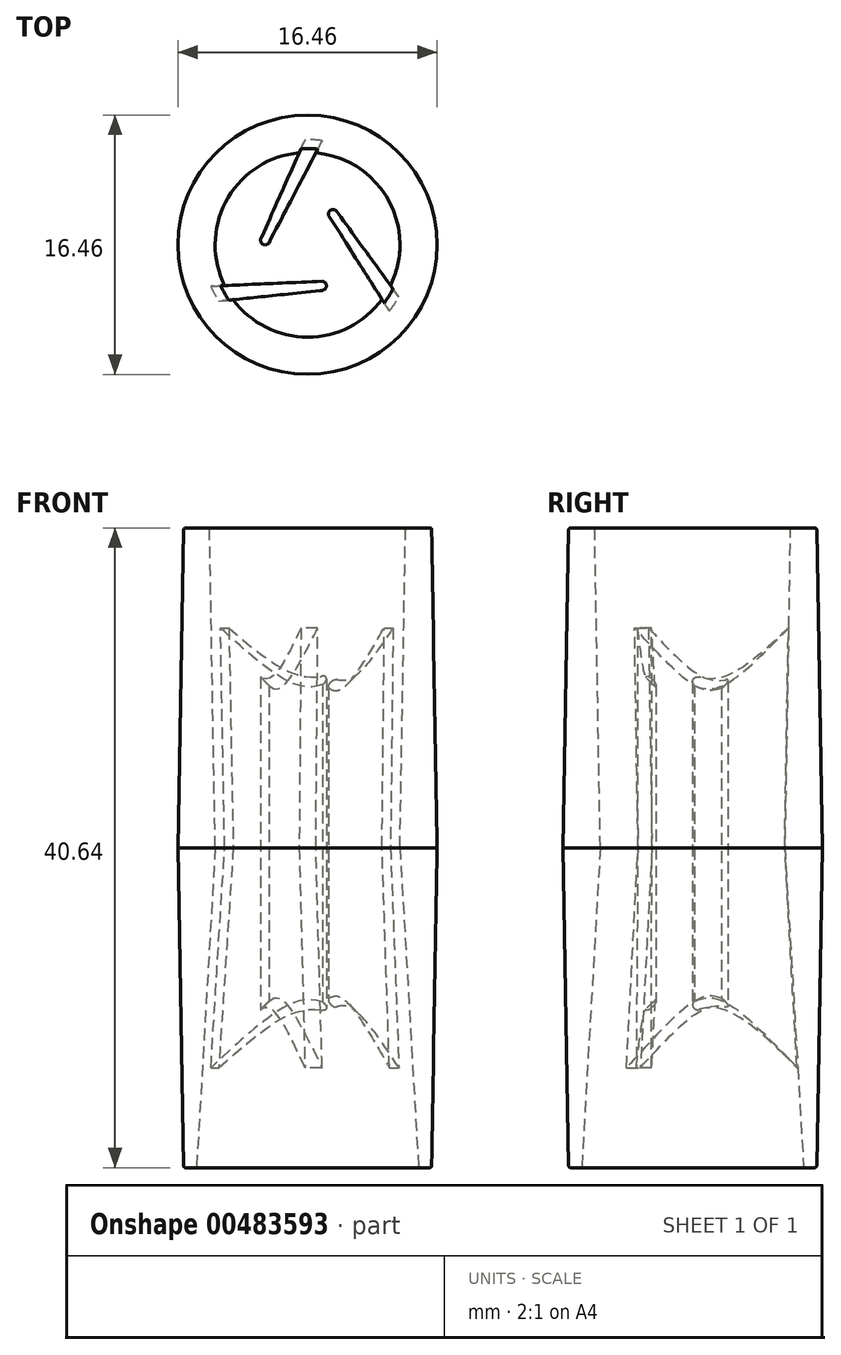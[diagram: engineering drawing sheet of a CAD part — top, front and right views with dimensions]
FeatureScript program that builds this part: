
annotation { "Feature Type Name" : "Feature", "Feature Type Description" : "" }
export const myFeature = defineFeature(function(context is Context, id is Id, definition is map)
    precondition{}
    {
        {
            var Q0;
            Q0=qCreatedBy(makeId("Front.planeOp"),FACE);
            var sketch = newSketch(context, id + "F0", { "sketchPlane" : qUnion([Q0])});
            skLineSegment(sketch, "E0", {"start": v(0, 30.91) * mm, "end": v(0, -20.42) * mm, "construction": true});
            skLineSegment(sketch, "E1", {"start": v(-15.28, 0) * mm, "end": v(16.53, 0) * mm, "construction": true});
            skLineSegment(sketch, "E2", {"start": v(8.23, 0) * mm, "end": v(7.88, -20.2) * mm});
            skLineSegment(sketch, "E3", {"start": v(7.75, -20.32) * mm, "end": v(7.17, -20.32) * mm});
            skLineSegment(sketch, "E4", {"start": v(7.04, -20.2) * mm, "end": v(5.87, 0) * mm});
            skLineSegment(sketch, "E5", {"start": v(5.87, 0) * mm, "end": v(6.22, 20.2) * mm});
            skLineSegment(sketch, "E6", {"start": v(6.35, 20.32) * mm, "end": v(7.75, 20.32) * mm});
            skLineSegment(sketch, "E7", {"start": v(8.23, 0) * mm, "end": v(7.88, 20.2) * mm});
            skPoint(sketch, "E8.visualSharp", {"position": v(7.87, -20.32) * mm});
            skArc(sketch, "E8.filletArc", {"start": v(7.75, -20.32) * mm, "mid": v(7.84, -20.28) * mm, "end": v(7.88, -20.2) * mm});
            skPoint(sketch, "E9.visualSharp", {"position": v(7.05, -20.32) * mm});
            skArc(sketch, "E9.filletArc", {"start": v(7.04, -20.2) * mm, "mid": v(7.08, -20.29) * mm, "end": v(7.17, -20.32) * mm});
            skPoint(sketch, "E10.visualSharp", {"position": v(6.22, 20.32) * mm});
            skArc(sketch, "E10.filletArc", {"start": v(6.35, 20.32) * mm, "mid": v(6.26, 20.28) * mm, "end": v(6.22, 20.2) * mm});
            skPoint(sketch, "E11.visualSharp", {"position": v(7.87, 20.32) * mm});
            skArc(sketch, "E11.filletArc", {"start": v(7.88, 20.2) * mm, "mid": v(7.84, 20.28) * mm, "end": v(7.75, 20.32) * mm});
            skPoint(sketch, "E12", {"position": v(6.68, -13.97) * mm});
            skPoint(sketch, "E13", {"position": v(6.11, 13.97) * mm});
            skSolve(sketch);
        }
        {
            var Q0;
            Q0=makeQuery(id+"F0.imprint","IMPRINT",FACE,{"disambiguationData":[TD([[makeQuery(id+"F0.imprint","IMPRINT",EDGE,{"derivedFrom":sQuery(id+"F0.wireOp",EDGE,"E2")}),-1.0]])]});
            var Q1;
            Q1=sQuery(id+"F0.wireOp",EDGE,"E0");
            revolve(context, id + "F1", {"entities" : qUnion([Q0]), "axis" : qUnion([Q1]), "revolveType" : RevolveType.FULL});
        }
        {
            var Q0;
            Q0=qCreatedBy(makeId("Top.planeOp"),FACE);
            var sketch = newSketch(context, id + "F2", { "sketchPlane" : qUnion([Q0])});
            skCircle(sketch, "E14.0", {"center": v(-0.06, -0.12) * mm, "radius": 7.16 * mm});
            skCircle(sketch, "E15", {"center": v(-0.06, -0.12) * mm, "radius": 2.41 * mm, "construction": true});
            skLineSegment(sketch, "E16", {"start": v(1.1, 6.95) * mm, "end": v(-2.46, 0.11) * mm});
            skLineSegment(sketch, "E17", {"start": v(-2.9, 0.53) * mm, "end": v(0, 7.04) * mm});
            skArc(sketch, "E18", {"start": v(-2.96, 0.4) * mm, "mid": v(-2.84, 0.04) * mm, "end": v(-2.46, 0.11) * mm});
            skLineSegment(sketch, "E19.1.0", {"start": v(5.49, -4.66) * mm, "end": v(1.35, 1.84) * mm});
            skLineSegment(sketch, "E19.1.1", {"start": v(1.93, 2.02) * mm, "end": v(6.12, -3.75) * mm});
            skArc(sketch, "E19.1.2", {"start": v(1.85, 2.13) * mm, "mid": v(1.47, 2.21) * mm, "end": v(1.35, 1.84) * mm});
            skLineSegment(sketch, "E19.2.0", {"start": v(-6.76, -2.66) * mm, "end": v(0.94, -2.32) * mm});
            skLineSegment(sketch, "E19.2.1", {"start": v(0.8, -2.91) * mm, "end": v(-6.29, -3.65) * mm});
            skArc(sketch, "E19.2.2", {"start": v(0.93, -2.9) * mm, "mid": v(1.2, -2.61) * mm, "end": v(0.94, -2.32) * mm});
            skLineSegment(sketch, "E19.anchor1", {"start": v(-0.06, -0.12) * mm, "end": v(-2.46, 0.11) * mm, "construction": true});
            skLineSegment(sketch, "E19.anchor2", {"start": v(-0.06, -0.12) * mm, "end": v(0.94, -2.32) * mm, "construction": true});
            skLineSegment(sketch, "E20", {"start": v(1.85, 2.13) * mm, "end": v(1.93, 2.02) * mm});
            skLineSegment(sketch, "E21", {"start": v(-2.96, 0.4) * mm, "end": v(-2.9, 0.53) * mm});
            skLineSegment(sketch, "E22", {"start": v(0.93, -2.9) * mm, "end": v(0.8, -2.91) * mm});
            skSolve(sketch);
        }
        {
            var Q0;
            {var subQ0=sQuery(id+"F2.wireOp",EDGE,"E16");Q0=makeQuery(id+"F2.imprint","IMPRINT",FACE,{"disambiguationData":[TD([[makeQuery(id+"F2.imprint","IMPRINT",EDGE,{"derivedFrom":subQ0}),-1.0]])]});}
            var Q1;
            {var subQ0=sQuery(id+"F2.wireOp",EDGE,"E19.1.0");Q1=makeQuery(id+"F2.imprint","IMPRINT",FACE,{"disambiguationData":[TD([[makeQuery(id+"F2.imprint","IMPRINT",EDGE,{"derivedFrom":subQ0}),-1.0]])]});}
            var Q2;
            {var subQ0=sQuery(id+"F2.wireOp",EDGE,"E19.2.0");Q2=makeQuery(id+"F2.imprint","IMPRINT",FACE,{"disambiguationData":[TD([[makeQuery(id+"F2.imprint","IMPRINT",EDGE,{"derivedFrom":subQ0}),-1.0]])]});}
            extrude(context, id + "F3", {"entities" : qUnion([Q0, Q1, Q2]), "operationType" : NewBodyOperationType.ADD, "endBound" : BoundingType.SYMMETRIC, "depth" : 27.94 * mm, "offsetDistance" : 25.4 * mm});
        }
        {
            var Q0;
            Q0=qCreatedBy(makeId("Front.planeOp"),FACE);
            var sketch = newSketch(context, id + "F4", { "sketchPlane" : qUnion([Q0])});
            skPoint(sketch, "E23.0", {"position": v(6.68, -13.97) * mm});
            skPoint(sketch, "E24.0", {"position": v(6.11, 13.97) * mm});
            skLineSegment(sketch, "E25", {"start": v(0, -13.97) * mm, "end": v(6.68, -13.97) * mm});
            skLineSegment(sketch, "E26", {"start": v(0, -13.97) * mm, "end": v(0, -7.3) * mm});
            skLineSegment(sketch, "E27", {"start": v(0, -7.3) * mm, "end": v(6.68, -13.97) * mm});
            skLineSegment(sketch, "E28", {"start": v(0, 13.97) * mm, "end": v(6.11, 13.97) * mm});
            skLineSegment(sketch, "E29", {"start": v(0, 13.97) * mm, "end": v(0, 7.86) * mm});
            skLineSegment(sketch, "E30", {"start": v(0, 7.86) * mm, "end": v(6.11, 13.97) * mm});
            skSolve(sketch);
        }
        {
            var Q0;
            Q0=makeQuery(id+"F4.imprint","IMPRINT",FACE,{"disambiguationData":[TD([[makeQuery(id+"F4.imprint","IMPRINT",EDGE,{"derivedFrom":sQuery(id+"F4.wireOp",EDGE,"E28")}),-1.0]])]});
            var Q1;
            Q1=makeQuery(id+"F4.imprint","IMPRINT",FACE,{"disambiguationData":[TD([[makeQuery(id+"F4.imprint","IMPRINT",EDGE,{"derivedFrom":sQuery(id+"F4.wireOp",EDGE,"E25")}),1.0]])]});
            var Q2;
            Q2=sQuery(id+"F0.wireOp",EDGE,"E0");
            revolve(context, id + "F5", {"operationType" : NewBodyOperationType.REMOVE, "entities" : qUnion([Q0, Q1]), "axis" : qUnion([Q2]), "revolveType" : RevolveType.FULL, "oppositeDirection" : true});
        }
    });
